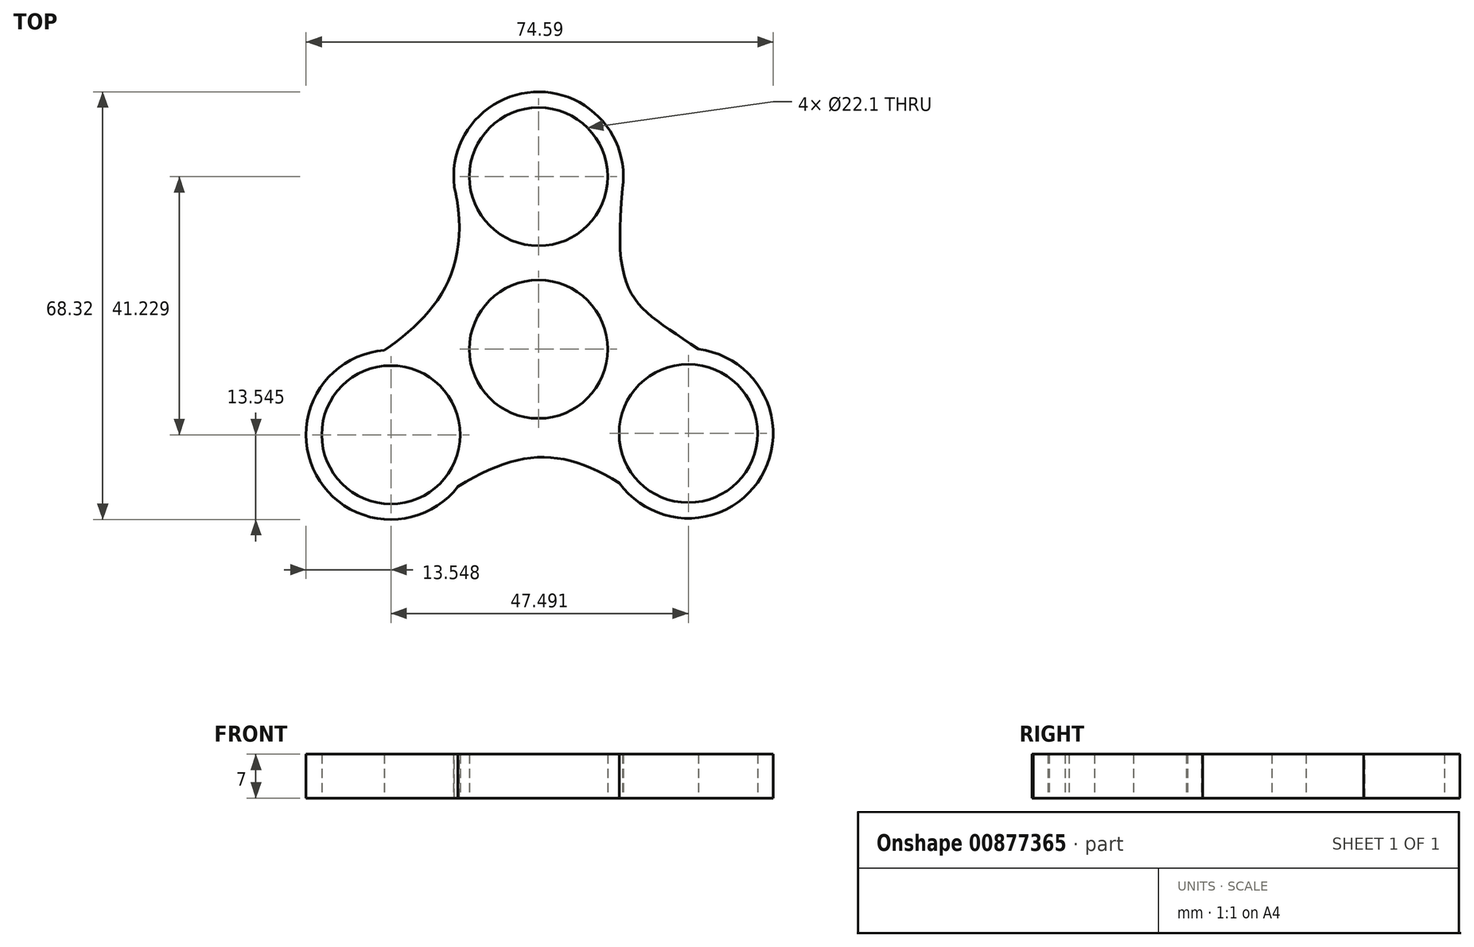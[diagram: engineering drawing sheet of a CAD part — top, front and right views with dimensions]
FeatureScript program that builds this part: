
annotation { "Feature Type Name" : "Feature", "Feature Type Description" : "" }
export const myFeature = defineFeature(function(context is Context, id is Id, definition is map)
    precondition{}
    {
        {
            var Q0;
            Q0=qCreatedBy(makeId("Top.planeOp"),FACE);
            var sketch = newSketch(context, id + "F0", { "sketchPlane" : qUnion([Q0])});
            skCircle(sketch, "E0", {"center": v(0, 0) * mm, "radius": 11.05 * mm});
            skCircle(sketch, "E1", {"center": v(0, 0) * mm, "radius": 13.55 * mm});
            skCircle(sketch, "E2", {"center": v(0, 27.57) * mm, "radius": 11.05 * mm});
            skCircle(sketch, "E3", {"center": v(0, 27.57) * mm, "radius": 13.55 * mm});
            skCircle(sketch, "E4.1.0", {"center": v(-23.57, -13.65) * mm, "radius": 11.05 * mm});
            skCircle(sketch, "E4.1.1", {"center": v(-23.57, -13.65) * mm, "radius": 13.55 * mm});
            skCircle(sketch, "E4.2.0", {"center": v(23.92, -13.45) * mm, "radius": 11.05 * mm});
            skCircle(sketch, "E4.2.1", {"center": v(23.92, -13.45) * mm, "radius": 13.55 * mm});
            skPoint(sketch, "E4.center", {"position": v(0.12, 0.15) * mm});
            skFitSpline(sketch, "E5", {"points": [v(-24.61, -0.14) * mm, v(-13.45, 25.95) * mm], "startDerivative": vector(24.14, 16.55) * mm, "endDerivative": vector(-9.26, 39.8) * mm});
            skFitSpline(sketch, "E6", {"points": [v(-12.86, -21.95) * mm, v(12.9, -21.34) * mm], "startDerivative": vector(29.76, 18.52) * mm, "endDerivative": vector(27.1, -16.68) * mm});
            skFitSpline(sketch, "E7", {"points": [v(13.42, 25.73) * mm, v(25.53, 0) * mm], "startDerivative": vector(-5.5, -56.12) * mm, "endDerivative": vector(29.7, -21.06) * mm});
            skSolve(sketch);
        }
        {
            var Q0;
            Q0=makeQuery(id+"F0.imprint","IMPRINT",FACE,{"disambiguationData":[TD([[makeQuery(id+"F0.imprint","IMPRINT",EDGE,{"derivedFrom":sQuery(id+"F0.wireOp",EDGE,"E4.1.0")}),-1.0]])]});
            var Q1;
            Q1=makeQuery(id+"F0.imprint","IMPRINT",FACE,{"disambiguationData":[TD([[makeQuery(id+"F0.imprint","IMPRINT",EDGE,{"derivedFrom":sQuery(id+"F0.wireOp",EDGE,"E2")}),-1.0]])]});
            var Q2;
            Q2=makeQuery(id+"F0.imprint","IMPRINT",FACE,{"disambiguationData":[TD([[makeQuery(id+"F0.imprint","IMPRINT",EDGE,{"derivedFrom":sQuery(id+"F0.wireOp",EDGE,"E4.2.0")}),-1.0]])]});
            var Q3;
            Q3=makeQuery(id+"F0.imprint","IMPRINT",FACE,{"disambiguationData":[TD([[makeQuery(id+"F0.imprint","IMPRINT",EDGE,{"derivedFrom":sQuery(id+"F0.wireOp",EDGE,"E1")}),-1.0]])]});
            var Q4;
            Q4=makeQuery(id+"F0.imprint","IMPRINT",FACE,{"disambiguationData":[TD([[makeQuery(id+"F0.imprint","IMPRINT",EDGE,{"derivedFrom":sQuery(id+"F0.wireOp",EDGE,"E0")}),-1.0]])]});
            extrude(context, id + "F1", {"entities" : qUnion([Q0, Q1, Q2, Q3, Q4]), "depth" : 7 * mm, "offsetDistance" : 25 * mm});
        }
    });
